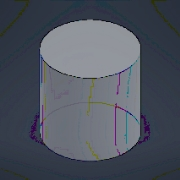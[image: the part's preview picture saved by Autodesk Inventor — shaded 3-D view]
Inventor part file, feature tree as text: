
AUTODESK INVENTOR PART (.ipt)
format: ipt  version: 2025.3 (Build 293356000, 356)  size: 129,024 bytes
history: native  units: mm
features: extrude x1, sketch x1
ambient origin geometry x8: Origin, YZ Plane, XZ Plane, XY Plane, X Axis, Y Axis, Z Axis, Center Point
bodies: Solid1 (feature_tree)
feature tree (2):
  extrude  "Extrusion1"  [1 undecoded]
  sketch  "Sketch1"  dims[d1=100.0mm d2=0.0mm]
note: 1 required parameter value undecoded (feature->parameter linkage not recoverable at this tier; creation-order binding heuristic only, values carry confidence <= 0.55)
